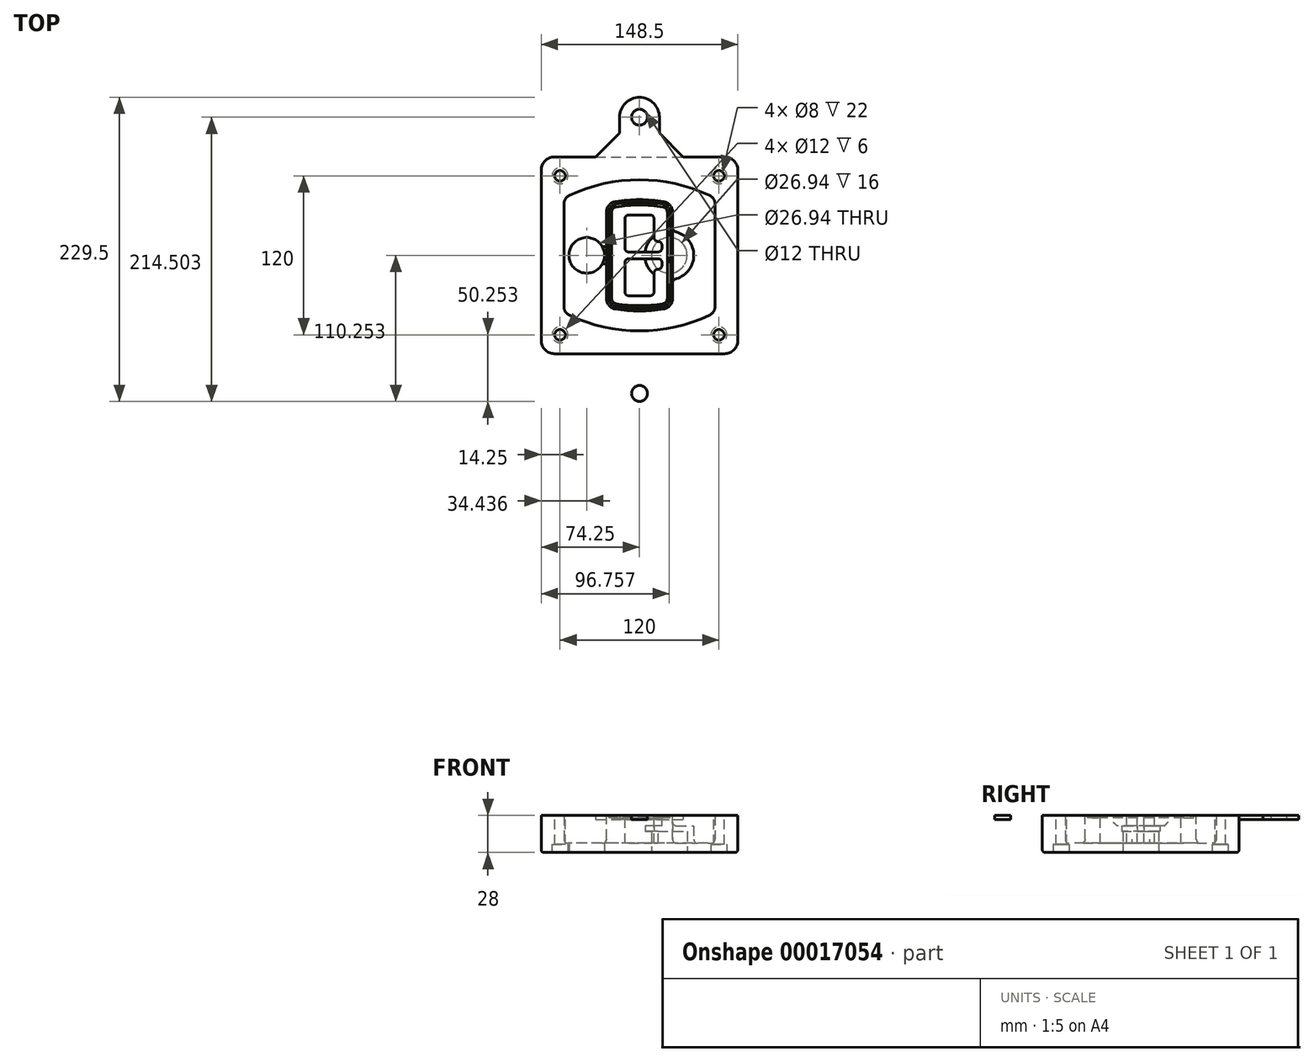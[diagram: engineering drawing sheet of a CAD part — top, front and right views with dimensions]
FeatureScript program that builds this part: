
annotation { "Feature Type Name" : "Feature", "Feature Type Description" : "" }
export const myFeature = defineFeature(function(context is Context, id is Id, definition is map)
    precondition{}
    {
        {
            var Q0;
            Q0=qCreatedBy(makeId("Top.planeOp"),FACE);
            var sketch = newSketch(context, id + "F0", { "sketchPlane" : qUnion([Q0])});
            skPoint(sketch, "E0.rect.middle", {"position": v(0, 0) * mm});
            skLineSegment(sketch, "E1.bottom", {"start": v(24.05, 28.38) * mm, "end": v(152.55, 28.38) * mm});
            skLineSegment(sketch, "E1.top", {"start": v(24.05, 176.88) * mm, "end": v(152.55, 176.88) * mm});
            skLineSegment(sketch, "E1.left", {"start": v(14.05, 38.38) * mm, "end": v(14.05, 166.88) * mm});
            skLineSegment(sketch, "E1.right", {"start": v(162.55, 38.38) * mm, "end": v(162.55, 166.88) * mm});
            skLineSegment(sketch, "E2", {"start": v(14.05, 176.88) * mm, "end": v(162.55, 28.38) * mm, "construction": true});
            skLineSegment(sketch, "E3", {"start": v(162.55, 176.88) * mm, "end": v(14.05, 28.38) * mm, "construction": true});
            skCircle(sketch, "E4", {"center": v(28.3, 162.63) * mm, "radius": 4 * mm});
            skCircle(sketch, "E5", {"center": v(148.3, 162.63) * mm, "radius": 4 * mm});
            skCircle(sketch, "E6", {"center": v(148.3, 42.63) * mm, "radius": 4 * mm});
            skCircle(sketch, "E7", {"center": v(28.3, 42.63) * mm, "radius": 4 * mm});
            skLineSegment(sketch, "E8", {"start": v(28.3, 162.63) * mm, "end": v(148.3, 162.63) * mm, "construction": true});
            skLineSegment(sketch, "E9", {"start": v(148.3, 162.63) * mm, "end": v(148.3, 42.63) * mm, "construction": true});
            skLineSegment(sketch, "E10", {"start": v(148.3, 42.63) * mm, "end": v(28.3, 42.63) * mm, "construction": true});
            skLineSegment(sketch, "E11", {"start": v(28.3, 42.63) * mm, "end": v(28.3, 162.63) * mm, "construction": true});
            skLineSegment(sketch, "E12", {"start": v(28.3, 141.46) * mm, "end": v(28.3, 63.8) * mm});
            skLineSegment(sketch, "E13", {"start": v(148.3, 141.46) * mm, "end": v(148.3, 63.8) * mm});
            skArc(sketch, "E14", {"start": v(142.56, 150.51) * mm, "mid": v(88.3, 162.63) * mm, "end": v(34.04, 150.51) * mm});
            skArc(sketch, "E15", {"start": v(34.04, 54.75) * mm, "mid": v(88.3, 42.63) * mm, "end": v(142.56, 54.75) * mm});
            skLineSegment(sketch, "E16", {"start": v(28.3, 102.63) * mm, "end": v(148.3, 102.63) * mm, "construction": true});
            skPoint(sketch, "E17.visualSharp", {"position": v(28.3, 57.63) * mm});
            skArc(sketch, "E17.filletArc", {"start": v(28.3, 63.8) * mm, "mid": v(29.86, 58.44) * mm, "end": v(34.04, 54.75) * mm});
            skPoint(sketch, "E18.visualSharp", {"position": v(28.3, 147.63) * mm});
            skArc(sketch, "E18.filletArc", {"start": v(34.04, 150.51) * mm, "mid": v(29.86, 146.82) * mm, "end": v(28.3, 141.46) * mm});
            skPoint(sketch, "E19.visualSharp", {"position": v(148.3, 147.63) * mm});
            skArc(sketch, "E19.filletArc", {"start": v(148.3, 141.46) * mm, "mid": v(146.74, 146.82) * mm, "end": v(142.56, 150.51) * mm});
            skPoint(sketch, "E20.visualSharp", {"position": v(148.3, 57.63) * mm});
            skArc(sketch, "E20.filletArc", {"start": v(142.56, 54.75) * mm, "mid": v(146.74, 58.44) * mm, "end": v(148.3, 63.8) * mm});
            skPoint(sketch, "E21.visualSharp", {"position": v(14.05, 176.88) * mm});
            skArc(sketch, "E21.filletArc", {"start": v(24.05, 176.88) * mm, "mid": v(16.98, 173.95) * mm, "end": v(14.05, 166.88) * mm});
            skPoint(sketch, "E22.visualSharp", {"position": v(162.55, 176.88) * mm});
            skArc(sketch, "E22.filletArc", {"start": v(162.55, 166.88) * mm, "mid": v(159.62, 173.95) * mm, "end": v(152.55, 176.88) * mm});
            skPoint(sketch, "E23.visualSharp", {"position": v(162.55, 28.38) * mm});
            skArc(sketch, "E23.filletArc", {"start": v(152.55, 28.38) * mm, "mid": v(159.62, 31.31) * mm, "end": v(162.55, 38.38) * mm});
            skPoint(sketch, "E24.visualSharp", {"position": v(14.05, 28.38) * mm});
            skArc(sketch, "E24.filletArc", {"start": v(14.05, 38.38) * mm, "mid": v(16.98, 31.31) * mm, "end": v(24.05, 28.38) * mm});
            skArc(sketch, "E25.0", {"start": v(145.3, 141.46) * mm, "mid": v(144.2, 145.22) * mm, "end": v(141.28, 147.8) * mm});
            skLineSegment(sketch, "E25.1", {"start": v(145.3, 141.46) * mm, "end": v(145.3, 63.8) * mm});
            skArc(sketch, "E25.2", {"start": v(141.28, 57.47) * mm, "mid": v(144.2, 60.05) * mm, "end": v(145.3, 63.8) * mm});
            skArc(sketch, "E25.3", {"start": v(35.32, 57.47) * mm, "mid": v(88.3, 45.63) * mm, "end": v(141.28, 57.47) * mm});
            skArc(sketch, "E25.4", {"start": v(31.3, 63.8) * mm, "mid": v(32.4, 60.05) * mm, "end": v(35.32, 57.47) * mm});
            skArc(sketch, "E25.5", {"start": v(141.28, 147.8) * mm, "mid": v(88.3, 159.63) * mm, "end": v(35.32, 147.8) * mm});
            skLineSegment(sketch, "E25.6", {"start": v(31.3, 141.46) * mm, "end": v(31.3, 63.8) * mm});
            skArc(sketch, "E25.7", {"start": v(35.32, 147.8) * mm, "mid": v(32.4, 145.22) * mm, "end": v(31.3, 141.46) * mm});
            skArc(sketch, "E26.0", {"start": v(32.34, 154.13) * mm, "mid": v(26.48, 148.97) * mm, "end": v(24.3, 141.46) * mm});
            skArc(sketch, "E26.1", {"start": v(144.26, 154.13) * mm, "mid": v(88.3, 166.63) * mm, "end": v(32.34, 154.13) * mm});
            skArc(sketch, "E26.2", {"start": v(152.3, 141.46) * mm, "mid": v(150.12, 148.97) * mm, "end": v(144.26, 154.13) * mm});
            skLineSegment(sketch, "E26.3", {"start": v(152.3, 141.46) * mm, "end": v(152.3, 63.8) * mm});
            skArc(sketch, "E26.4", {"start": v(144.26, 51.13) * mm, "mid": v(150.12, 56.3) * mm, "end": v(152.3, 63.8) * mm});
            skLineSegment(sketch, "E26.5", {"start": v(24.3, 141.46) * mm, "end": v(24.3, 63.8) * mm});
            skArc(sketch, "E26.6", {"start": v(32.34, 51.13) * mm, "mid": v(88.3, 38.63) * mm, "end": v(144.26, 51.13) * mm});
            skArc(sketch, "E26.7", {"start": v(24.3, 63.8) * mm, "mid": v(26.48, 56.3) * mm, "end": v(32.34, 51.13) * mm});
            skSolve(sketch);
        }
        {
            var Q0;
            Q0=makeQuery(id+"F0.imprint","IMPRINT",FACE,{"disambiguationData":[TD([[makeQuery(id+"F0.imprint","IMPRINT",EDGE,{"derivedFrom":sQuery(id+"F0.wireOp",EDGE,"E1.bottom")}),1.0]])]});
            var Q1;
            Q1=makeQuery(id+"F0.imprint","IMPRINT",FACE,{"disambiguationData":[TD([[makeQuery(id+"F0.imprint","IMPRINT",EDGE,{"derivedFrom":sQuery(id+"F0.wireOp",EDGE,"E12")}),1.0]])]});
            var Q2;
            Q2=makeQuery(id+"F0.imprint","IMPRINT",FACE,{"disambiguationData":[TD([[makeQuery(id+"F0.imprint","IMPRINT",EDGE,{"derivedFrom":sQuery(id+"F0.wireOp",EDGE,"E25.0")}),1.0]])]});
            var Q3;
            Q3=makeQuery(id+"F0.imprint","IMPRINT",FACE,{"disambiguationData":[TD([[makeQuery(id+"F0.imprint","IMPRINT",EDGE,{"derivedFrom":sQuery(id+"F0.wireOp",EDGE,"E12")}),-1.0]])]});
            extrude(context, id + "F1", {"entities" : qUnion([Q0, Q1, Q2, Q3]), "oppositeDirection" : true, "depth" : 25 * mm});
        }
        {
            var Q0;
            Q0=makeQuery(id+"F0.imprint","IMPRINT",FACE,{"disambiguationData":[TD([[makeQuery(id+"F0.imprint","IMPRINT",EDGE,{"derivedFrom":sQuery(id+"F0.wireOp",EDGE,"E12")}),1.0]])]});
            extrude(context, id + "F2", {"entities" : qUnion([Q0]), "operationType" : NewBodyOperationType.ADD, "depth" : 3 * mm});
        }
        {
            var Q0;
            Q0=makeQuery(id+"F0.imprint","IMPRINT",FACE,{"disambiguationData":[TD([[makeQuery(id+"F0.imprint","IMPRINT",EDGE,{"derivedFrom":sQuery(id+"F0.wireOp",EDGE,"E25.0")}),1.0]])]});
            extrude(context, id + "F3", {"entities" : qUnion([Q0]), "operationType" : NewBodyOperationType.REMOVE, "oppositeDirection" : true, "depth" : 18 * mm});
        }
        {
            var Q0;
            Q0=makeQuery(id+"F2.opExtrude","CAP_FACE",FACE,{"disambiguationData":[OSD([sQuery(id+"F0.wireOp",EDGE,"E12"),sQuery(id+"F0.wireOp",EDGE,"E13"),sQuery(id+"F0.wireOp",EDGE,"E14"),sQuery(id+"F0.wireOp",EDGE,"E15"),sQuery(id+"F0.wireOp",EDGE,"E17.filletArc"),sQuery(id+"F0.wireOp",EDGE,"E18.filletArc"),sQuery(id+"F0.wireOp",EDGE,"E19.filletArc"),sQuery(id+"F0.wireOp",EDGE,"E20.filletArc"),sQuery(id+"F0.wireOp",EDGE,"E25.0"),sQuery(id+"F0.wireOp",EDGE,"E25.1"),sQuery(id+"F0.wireOp",EDGE,"E25.2"),sQuery(id+"F0.wireOp",EDGE,"E25.3"),sQuery(id+"F0.wireOp",EDGE,"E25.4"),sQuery(id+"F0.wireOp",EDGE,"E25.5"),sQuery(id+"F0.wireOp",EDGE,"E25.6"),sQuery(id+"F0.wireOp",EDGE,"E25.7")])],"isStart":false});
            var sketch = newSketch(context, id + "F4", { "sketchPlane" : qUnion([Q0])});
            skArc(sketch, "E27.0", {"start": v(69.96, 62.18) * mm, "mid": v(88.3, 60.63) * mm, "end": v(106.64, 62.18) * mm});
            skArc(sketch, "E28.0", {"start": v(106.64, 143.09) * mm, "mid": v(88.3, 144.63) * mm, "end": v(69.96, 143.09) * mm});
            skLineSegment(sketch, "E29", {"start": v(63.3, 135.2) * mm, "end": v(63.3, 70.07) * mm});
            skLineSegment(sketch, "E30", {"start": v(113.3, 135.2) * mm, "end": v(113.3, 70.07) * mm});
            skLineSegment(sketch, "E31", {"start": v(63.3, 141.74) * mm, "end": v(113.3, 141.74) * mm, "construction": true});
            skLineSegment(sketch, "E32", {"start": v(63.3, 63.52) * mm, "end": v(113.3, 63.52) * mm, "construction": true});
            skPoint(sketch, "E33.visualSharp", {"position": v(63.3, 141.74) * mm});
            skArc(sketch, "E33.filletArc", {"start": v(69.96, 143.09) * mm, "mid": v(65.19, 140.36) * mm, "end": v(63.3, 135.2) * mm});
            skPoint(sketch, "E34.visualSharp", {"position": v(113.3, 141.74) * mm});
            skArc(sketch, "E34.filletArc", {"start": v(113.3, 135.2) * mm, "mid": v(111.41, 140.36) * mm, "end": v(106.64, 143.09) * mm});
            skPoint(sketch, "E35.visualSharp", {"position": v(113.3, 63.52) * mm});
            skArc(sketch, "E35.filletArc", {"start": v(106.64, 62.18) * mm, "mid": v(111.41, 64.9) * mm, "end": v(113.3, 70.07) * mm});
            skPoint(sketch, "E36.visualSharp", {"position": v(63.3, 63.52) * mm});
            skArc(sketch, "E36.filletArc", {"start": v(63.3, 70.07) * mm, "mid": v(65.19, 64.9) * mm, "end": v(69.96, 62.18) * mm});
            skArc(sketch, "E37.0", {"start": v(141.28, 147.8) * mm, "mid": v(88.3, 159.63) * mm, "end": v(35.32, 147.8) * mm});
            skArc(sketch, "E37.1", {"start": v(35.32, 147.8) * mm, "mid": v(32.4, 145.22) * mm, "end": v(31.3, 141.46) * mm});
            skLineSegment(sketch, "E37.2", {"start": v(31.3, 141.46) * mm, "end": v(31.3, 63.8) * mm});
            skArc(sketch, "E37.3", {"start": v(31.3, 63.8) * mm, "mid": v(32.4, 60.05) * mm, "end": v(35.32, 57.47) * mm});
            skArc(sketch, "E37.4", {"start": v(35.32, 57.47) * mm, "mid": v(88.3, 45.63) * mm, "end": v(141.28, 57.47) * mm});
            skArc(sketch, "E37.5", {"start": v(141.28, 57.47) * mm, "mid": v(144.2, 60.05) * mm, "end": v(145.3, 63.8) * mm});
            skLineSegment(sketch, "E37.6", {"start": v(145.3, 141.46) * mm, "end": v(145.3, 63.8) * mm});
            skArc(sketch, "E37.7", {"start": v(145.3, 141.46) * mm, "mid": v(144.2, 145.22) * mm, "end": v(141.28, 147.8) * mm});
            skLineSegment(sketch, "E38.0", {"start": v(111.3, 135.2) * mm, "end": v(111.3, 70.07) * mm});
            skArc(sketch, "E38.1", {"start": v(106.3, 64.15) * mm, "mid": v(109.88, 66.2) * mm, "end": v(111.3, 70.07) * mm});
            skArc(sketch, "E38.2", {"start": v(70.3, 64.15) * mm, "mid": v(88.3, 62.63) * mm, "end": v(106.3, 64.15) * mm});
            skArc(sketch, "E38.3", {"start": v(65.3, 70.07) * mm, "mid": v(66.72, 66.2) * mm, "end": v(70.3, 64.15) * mm});
            skLineSegment(sketch, "E38.4", {"start": v(65.3, 135.2) * mm, "end": v(65.3, 70.07) * mm});
            skArc(sketch, "E38.5", {"start": v(111.3, 135.2) * mm, "mid": v(109.88, 139.07) * mm, "end": v(106.3, 141.11) * mm});
            skArc(sketch, "E38.6", {"start": v(70.3, 141.11) * mm, "mid": v(66.72, 139.07) * mm, "end": v(65.3, 135.2) * mm});
            skArc(sketch, "E38.7", {"start": v(106.3, 141.11) * mm, "mid": v(88.3, 142.63) * mm, "end": v(70.3, 141.11) * mm});
            skArc(sketch, "E39.0", {"start": v(109.3, 135.2) * mm, "mid": v(108.36, 137.78) * mm, "end": v(105.97, 139.14) * mm});
            skLineSegment(sketch, "E39.1", {"start": v(109.3, 135.2) * mm, "end": v(109.3, 70.07) * mm});
            skArc(sketch, "E39.2", {"start": v(105.97, 66.12) * mm, "mid": v(108.36, 67.49) * mm, "end": v(109.3, 70.07) * mm});
            skArc(sketch, "E39.3", {"start": v(70.63, 66.12) * mm, "mid": v(88.3, 64.63) * mm, "end": v(105.97, 66.12) * mm});
            skArc(sketch, "E39.4", {"start": v(67.3, 70.07) * mm, "mid": v(68.24, 67.49) * mm, "end": v(70.63, 66.12) * mm});
            skArc(sketch, "E39.5", {"start": v(105.97, 139.14) * mm, "mid": v(88.3, 140.63) * mm, "end": v(70.63, 139.14) * mm});
            skLineSegment(sketch, "E39.6", {"start": v(67.3, 135.2) * mm, "end": v(67.3, 70.07) * mm});
            skArc(sketch, "E39.7", {"start": v(70.63, 139.14) * mm, "mid": v(68.24, 137.78) * mm, "end": v(67.3, 135.2) * mm});
            skLineSegment(sketch, "E40", {"start": v(63.3, 102.63) * mm, "end": v(113.3, 102.63) * mm, "construction": true});
            skLineSegment(sketch, "E41", {"start": v(77.3, 108.13) * mm, "end": v(77.3, 130.13) * mm});
            skLineSegment(sketch, "E42", {"start": v(80.3, 133.13) * mm, "end": v(96.3, 133.13) * mm});
            skLineSegment(sketch, "E43", {"start": v(99.3, 130.13) * mm, "end": v(99.3, 116.13) * mm});
            skLineSegment(sketch, "E44", {"start": v(102.3, 113.13) * mm, "end": v(102.3, 113.13) * mm});
            skLineSegment(sketch, "E45", {"start": v(105.3, 110.13) * mm, "end": v(105.3, 108.13) * mm});
            skLineSegment(sketch, "E46", {"start": v(102.3, 105.13) * mm, "end": v(80.3, 105.13) * mm});
            skPoint(sketch, "E47.visualSharp", {"position": v(77.3, 133.13) * mm});
            skArc(sketch, "E47.filletArc", {"start": v(80.3, 133.13) * mm, "mid": v(78.18, 132.25) * mm, "end": v(77.3, 130.13) * mm});
            skPoint(sketch, "E48.visualSharp", {"position": v(99.3, 133.13) * mm});
            skArc(sketch, "E48.filletArc", {"start": v(99.3, 130.13) * mm, "mid": v(98.42, 132.25) * mm, "end": v(96.3, 133.13) * mm});
            skPoint(sketch, "E49.visualSharp", {"position": v(99.3, 113.13) * mm});
            skArc(sketch, "E49.filletArc", {"start": v(99.3, 116.13) * mm, "mid": v(100.18, 114.01) * mm, "end": v(102.3, 113.13) * mm});
            skPoint(sketch, "E50.visualSharp", {"position": v(105.3, 113.13) * mm});
            skArc(sketch, "E50.filletArc", {"start": v(105.3, 110.13) * mm, "mid": v(104.42, 112.25) * mm, "end": v(102.3, 113.13) * mm});
            skPoint(sketch, "E51.visualSharp", {"position": v(105.3, 105.13) * mm});
            skArc(sketch, "E51.filletArc", {"start": v(102.3, 105.13) * mm, "mid": v(104.42, 106.01) * mm, "end": v(105.3, 108.13) * mm});
            skPoint(sketch, "E52.visualSharp", {"position": v(77.3, 105.13) * mm});
            skArc(sketch, "E52.filletArc", {"start": v(77.3, 108.13) * mm, "mid": v(78.18, 106.01) * mm, "end": v(80.3, 105.13) * mm});
            skLineSegment(sketch, "E53.0.MirrorCS", {"start": v(102.3, 100.13) * mm, "end": v(80.3, 100.13) * mm});
            skArc(sketch, "E54.0.MirrorCS", {"start": v(77.3, 97.13) * mm, "mid": v(78.18, 99.25) * mm, "end": v(80.3, 100.13) * mm});
            skLineSegment(sketch, "E55.0.MirrorCS", {"start": v(77.3, 97.13) * mm, "end": v(77.3, 75.13) * mm});
            skArc(sketch, "E56.0.MirrorCS", {"start": v(80.3, 72.13) * mm, "mid": v(78.18, 73.01) * mm, "end": v(77.3, 75.13) * mm});
            skLineSegment(sketch, "E57.0.MirrorCS", {"start": v(80.3, 72.13) * mm, "end": v(96.3, 72.13) * mm});
            skArc(sketch, "E58.0.MirrorCS", {"start": v(99.3, 75.13) * mm, "mid": v(98.42, 73.01) * mm, "end": v(96.3, 72.13) * mm});
            skLineSegment(sketch, "E59.0.MirrorCS", {"start": v(99.3, 75.13) * mm, "end": v(99.3, 89.13) * mm});
            skArc(sketch, "E60.0.MirrorCS", {"start": v(99.3, 89.13) * mm, "mid": v(100.18, 91.25) * mm, "end": v(102.3, 92.13) * mm});
            skArc(sketch, "E61.0.MirrorCS", {"start": v(105.3, 95.13) * mm, "mid": v(104.42, 93.01) * mm, "end": v(102.3, 92.13) * mm});
            skLineSegment(sketch, "E62.0.MirrorCS", {"start": v(105.3, 95.13) * mm, "end": v(105.3, 97.13) * mm});
            skArc(sketch, "E63.0.MirrorCS", {"start": v(102.3, 100.13) * mm, "mid": v(104.42, 99.25) * mm, "end": v(105.3, 97.13) * mm});
            skSolve(sketch);
        }
        {
            var Q0;
            Q0=makeQuery(id+"F4.imprint","IMPRINT",FACE,{"disambiguationData":[TD([[makeQuery(id+"F4.imprint","IMPRINT",EDGE,{"derivedFrom":sQuery(id+"F4.wireOp",EDGE,"E27.0")}),1.0]])]});
            var Q1;
            Q1=makeQuery(id+"F4.imprint","IMPRINT",FACE,{"disambiguationData":[TD([[makeQuery(id+"F4.imprint","IMPRINT",EDGE,{"derivedFrom":sQuery(id+"F4.wireOp",EDGE,"E38.0")}),-1.0]])]});
            var Q2;
            Q2=makeQuery(id+"F4.imprint","IMPRINT",FACE,{"disambiguationData":[TD([[makeQuery(id+"F4.imprint","IMPRINT",EDGE,{"derivedFrom":sQuery(id+"F4.wireOp",EDGE,"E39.0")}),1.0]])]});
            extrude(context, id + "F5", {"entities" : qUnion([Q0, Q1, Q2]), "operationType" : NewBodyOperationType.ADD, "endBound" : BoundingType.UP_TO_NEXT, "oppositeDirection" : true, "depth" : 25 * mm});
        }
        {
            var Q0;
            Q0=makeQuery(id+"F4.imprint","IMPRINT",FACE,{"disambiguationData":[TD([[makeQuery(id+"F4.imprint","IMPRINT",EDGE,{"derivedFrom":sQuery(id+"F4.wireOp",EDGE,"E38.0")}),-1.0]])]});
            extrude(context, id + "F6", {"entities" : qUnion([Q0]), "operationType" : NewBodyOperationType.REMOVE, "oppositeDirection" : true, "depth" : 2 * mm});
        }
        {
            var Q0;
            Q0=makeQuery(id+"F1.opExtrude","CAP_FACE",FACE,{"disambiguationData":[OSD([sQuery(id+"F0.wireOp",EDGE,"E1.bottom"),sQuery(id+"F0.wireOp",EDGE,"E1.top"),sQuery(id+"F0.wireOp",EDGE,"E1.left"),sQuery(id+"F0.wireOp",EDGE,"E1.right"),sQuery(id+"F0.wireOp",EDGE,"E4"),sQuery(id+"F0.wireOp",EDGE,"E5"),sQuery(id+"F0.wireOp",EDGE,"E6"),sQuery(id+"F0.wireOp",EDGE,"E7"),sQuery(id+"F0.wireOp",EDGE,"E21.filletArc"),sQuery(id+"F0.wireOp",EDGE,"E22.filletArc"),sQuery(id+"F0.wireOp",EDGE,"E23.filletArc"),sQuery(id+"F0.wireOp",EDGE,"E24.filletArc")])],"isStart":false});
            var sketch = newSketch(context, id + "F7", { "sketchPlane" : qUnion([Q0])});
            skCircle(sketch, "E64", {"center": v(110.8, -102.63) * mm, "radius": 13.47 * mm});
            skCircle(sketch, "E65", {"center": v(48.49, -102.63) * mm, "radius": 13.47 * mm});
            skLineSegment(sketch, "E66", {"start": v(162.55, -102.63) * mm, "end": v(14.05, -102.63) * mm});
            skCircle(sketch, "E67", {"center": v(110.8, -102.63) * mm, "radius": 18.47 * mm});
            skCircle(sketch, "E68", {"center": v(148.3, -162.63) * mm, "radius": 6 * mm});
            skCircle(sketch, "E69", {"center": v(28.3, -162.63) * mm, "radius": 6 * mm});
            skCircle(sketch, "E70", {"center": v(28.3, -42.63) * mm, "radius": 6 * mm});
            skCircle(sketch, "E71", {"center": v(148.3, -42.63) * mm, "radius": 6 * mm});
            skSolve(sketch);
        }
        {
            var Q0;
            {var subQ1=sQuery(id+"F7.wireOp",EDGE,"E66");var subQ4=sQuery(id+"F7.wireOp",EDGE,"E64");var subQ6=makeQuery(id+"F7.imprint","INTERSECT",VERTEX,{"disambiguationData":[OD(0.0)],"derivedFrom":[subQ4,subQ1]});Q0=makeQuery(id+"F7.imprint","IMPRINT",FACE,{"disambiguationData":[TD([[makeQuery(id+"F7.imprint","IMPRINT",EDGE,{"disambiguationData":[TD([[subQ6,-1.0]])],"derivedFrom":subQ4}),-1.0]])]});}
            var Q1;
            {var subQ0=sQuery(id+"F7.wireOp",EDGE,"E66");var subQ1=sQuery(id+"F7.wireOp",EDGE,"E64");var subQ3=makeQuery(id+"F7.imprint","INTERSECT",VERTEX,{"disambiguationData":[OD(0.0)],"derivedFrom":[subQ1,subQ0]});Q1=makeQuery(id+"F7.imprint","IMPRINT",FACE,{"disambiguationData":[TD([[makeQuery(id+"F7.imprint","IMPRINT",EDGE,{"disambiguationData":[TD([[subQ3,-1.0]])],"derivedFrom":subQ1}),1.0]])]});}
            var Q2;
            {var subQ0=sQuery(id+"F7.wireOp",EDGE,"E66");var subQ1=sQuery(id+"F7.wireOp",EDGE,"E64");var subQ3=makeQuery(id+"F7.imprint","INTERSECT",VERTEX,{"disambiguationData":[OD(0.0)],"derivedFrom":[subQ1,subQ0]});Q2=makeQuery(id+"F7.imprint","IMPRINT",FACE,{"disambiguationData":[TD([[makeQuery(id+"F7.imprint","IMPRINT",EDGE,{"disambiguationData":[TD([[subQ3,1.0]])],"derivedFrom":subQ1}),1.0]])]});}
            var Q3;
            {var subQ1=sQuery(id+"F7.wireOp",EDGE,"E66");var subQ4=sQuery(id+"F7.wireOp",EDGE,"E64");var subQ6=makeQuery(id+"F7.imprint","INTERSECT",VERTEX,{"disambiguationData":[OD(0.0)],"derivedFrom":[subQ4,subQ1]});Q3=makeQuery(id+"F7.imprint","IMPRINT",FACE,{"disambiguationData":[TD([[makeQuery(id+"F7.imprint","IMPRINT",EDGE,{"disambiguationData":[TD([[subQ6,1.0]])],"derivedFrom":subQ4}),-1.0]])]});}
            extrude(context, id + "F8", {"entities" : qUnion([Q0, Q1, Q2, Q3]), "operationType" : NewBodyOperationType.ADD, "oppositeDirection" : true, "depth" : 20 * mm});
        }
        {
            var Q0;
            {var subQ0=sQuery(id+"F7.wireOp",EDGE,"E66");var subQ1=sQuery(id+"F7.wireOp",EDGE,"E64");var subQ3=makeQuery(id+"F7.imprint","INTERSECT",VERTEX,{"disambiguationData":[OD(0.0)],"derivedFrom":[subQ1,subQ0]});Q0=makeQuery(id+"F7.imprint","IMPRINT",FACE,{"disambiguationData":[TD([[makeQuery(id+"F7.imprint","IMPRINT",EDGE,{"disambiguationData":[TD([[subQ3,-1.0]])],"derivedFrom":subQ1}),1.0]])]});}
            var Q1;
            {var subQ0=sQuery(id+"F7.wireOp",EDGE,"E66");var subQ1=sQuery(id+"F7.wireOp",EDGE,"E64");var subQ3=makeQuery(id+"F7.imprint","INTERSECT",VERTEX,{"disambiguationData":[OD(0.0)],"derivedFrom":[subQ1,subQ0]});Q1=makeQuery(id+"F7.imprint","IMPRINT",FACE,{"disambiguationData":[TD([[makeQuery(id+"F7.imprint","IMPRINT",EDGE,{"disambiguationData":[TD([[subQ3,1.0]])],"derivedFrom":subQ1}),1.0]])]});}
            extrude(context, id + "F9", {"entities" : qUnion([Q0, Q1]), "operationType" : NewBodyOperationType.REMOVE, "oppositeDirection" : true, "depth" : 16 * mm});
        }
        {
            var Q0;
            {var subQ0=sQuery(id+"F7.wireOp",EDGE,"E66");var subQ1=sQuery(id+"F7.wireOp",EDGE,"E65");var subQ3=makeQuery(id+"F7.imprint","INTERSECT",VERTEX,{"disambiguationData":[OD(0.0)],"derivedFrom":[subQ1,subQ0]});Q0=makeQuery(id+"F7.imprint","IMPRINT",FACE,{"disambiguationData":[TD([[makeQuery(id+"F7.imprint","IMPRINT",EDGE,{"disambiguationData":[TD([[subQ3,-1.0]])],"derivedFrom":subQ1}),1.0]])]});}
            var Q1;
            {var subQ0=sQuery(id+"F7.wireOp",EDGE,"E66");var subQ1=sQuery(id+"F7.wireOp",EDGE,"E65");var subQ3=makeQuery(id+"F7.imprint","INTERSECT",VERTEX,{"disambiguationData":[OD(0.0)],"derivedFrom":[subQ1,subQ0]});Q1=makeQuery(id+"F7.imprint","IMPRINT",FACE,{"disambiguationData":[TD([[makeQuery(id+"F7.imprint","IMPRINT",EDGE,{"disambiguationData":[TD([[subQ3,1.0]])],"derivedFrom":subQ1}),1.0]])]});}
            extrude(context, id + "F10", {"entities" : qUnion([Q0, Q1]), "operationType" : NewBodyOperationType.REMOVE, "oppositeDirection" : true, "depth" : 25 * mm});
        }
        {
            var Q0;
            Q0=makeQuery(id+"F7.imprint","IMPRINT",FACE,{"disambiguationData":[TD([[makeQuery(id+"F7.imprint","IMPRINT",EDGE,{"derivedFrom":sQuery(id+"F7.wireOp",EDGE,"E68")}),1.0]])]});
            var Q1;
            Q1=makeQuery(id+"F7.imprint","IMPRINT",FACE,{"disambiguationData":[TD([[makeQuery(id+"F7.imprint","IMPRINT",EDGE,{"derivedFrom":makeQuery(id+"F1.opExtrude","CAP_EDGE",EDGE,{"disambiguationData":[OSD([sQuery(id+"F0.wireOp",EDGE,"E5")])],"isStart":false})}),-1.0]])]});
            var Q2;
            Q2=makeQuery(id+"F7.imprint","IMPRINT",FACE,{"disambiguationData":[TD([[makeQuery(id+"F7.imprint","IMPRINT",EDGE,{"derivedFrom":sQuery(id+"F7.wireOp",EDGE,"E69")}),1.0]])]});
            var Q3;
            Q3=makeQuery(id+"F7.imprint","IMPRINT",FACE,{"disambiguationData":[TD([[makeQuery(id+"F7.imprint","IMPRINT",EDGE,{"derivedFrom":makeQuery(id+"F1.opExtrude","CAP_EDGE",EDGE,{"disambiguationData":[OSD([sQuery(id+"F0.wireOp",EDGE,"E4")])],"isStart":false})}),-1.0]])]});
            var Q4;
            Q4=makeQuery(id+"F7.imprint","IMPRINT",FACE,{"disambiguationData":[TD([[makeQuery(id+"F7.imprint","IMPRINT",EDGE,{"derivedFrom":sQuery(id+"F7.wireOp",EDGE,"E70")}),1.0]])]});
            var Q5;
            Q5=makeQuery(id+"F7.imprint","IMPRINT",FACE,{"disambiguationData":[TD([[makeQuery(id+"F7.imprint","IMPRINT",EDGE,{"derivedFrom":makeQuery(id+"F1.opExtrude","CAP_EDGE",EDGE,{"disambiguationData":[OSD([sQuery(id+"F0.wireOp",EDGE,"E7")])],"isStart":false})}),-1.0]])]});
            var Q6;
            Q6=makeQuery(id+"F7.imprint","IMPRINT",FACE,{"disambiguationData":[TD([[makeQuery(id+"F7.imprint","IMPRINT",EDGE,{"derivedFrom":sQuery(id+"F7.wireOp",EDGE,"E71")}),1.0]])]});
            var Q7;
            Q7=makeQuery(id+"F7.imprint","IMPRINT",FACE,{"disambiguationData":[TD([[makeQuery(id+"F7.imprint","IMPRINT",EDGE,{"derivedFrom":makeQuery(id+"F1.opExtrude","CAP_EDGE",EDGE,{"disambiguationData":[OSD([sQuery(id+"F0.wireOp",EDGE,"E6")])],"isStart":false})}),-1.0]])]});
            extrude(context, id + "F11", {"entities" : qUnion([Q0, Q1, Q2, Q3, Q4, Q5, Q6, Q7]), "operationType" : NewBodyOperationType.REMOVE, "oppositeDirection" : true, "depth" : 6 * mm});
        }
        {
            var Q0;
            Q0=makeQuery(id+"F9.boolean.opBoolean","COPY",FACE,{"derivedFrom":makeQuery(id+"F9.opExtrude","CAP_FACE",FACE,{"disambiguationData":[OSD([sQuery(id+"F7.wireOp",EDGE,"E64")])],"isStart":false})});
            var sketch = newSketch(context, id + "F12", { "sketchPlane" : qUnion([Q0])});
            skArc(sketch, "E72.0", {"start": v(99.3, -88.19) * mm, "mid": v(94.75, -93.5) * mm, "end": v(92.5, -100.13) * mm});
            skArc(sketch, "E72.1", {"start": v(92.5, -105.13) * mm, "mid": v(94.75, -111.76) * mm, "end": v(99.3, -117.08) * mm});
            skLineSegment(sketch, "E73", {"start": v(92.5, -105.13) * mm, "end": v(102.3, -105.13) * mm});
            skLineSegment(sketch, "E74.0", {"start": v(102.3, -100.13) * mm, "end": v(92.5, -100.13) * mm});
            skArc(sketch, "E74.1", {"start": v(102.3, -100.13) * mm, "mid": v(104.42, -99.25) * mm, "end": v(105.3, -97.13) * mm});
            skLineSegment(sketch, "E74.2", {"start": v(105.3, -95.13) * mm, "end": v(105.3, -97.13) * mm});
            skArc(sketch, "E74.3", {"start": v(105.3, -95.13) * mm, "mid": v(104.42, -93.01) * mm, "end": v(102.3, -92.13) * mm});
            skArc(sketch, "E74.4", {"start": v(99.3, -89.13) * mm, "mid": v(100.18, -91.25) * mm, "end": v(102.3, -92.13) * mm});
            skLineSegment(sketch, "E74.5", {"start": v(99.3, -88.19) * mm, "end": v(99.3, -89.13) * mm});
            skLineSegment(sketch, "E74.7", {"start": v(102.3, -105.13) * mm, "end": v(92.5, -105.13) * mm});
            skArc(sketch, "E74.8", {"start": v(102.3, -105.13) * mm, "mid": v(104.42, -106.01) * mm, "end": v(105.3, -108.13) * mm});
            skLineSegment(sketch, "E74.9", {"start": v(105.3, -110.13) * mm, "end": v(105.3, -108.13) * mm});
            skArc(sketch, "E74.10", {"start": v(105.3, -110.13) * mm, "mid": v(104.42, -112.25) * mm, "end": v(102.3, -113.13) * mm});
            skArc(sketch, "E74.11", {"start": v(99.3, -116.13) * mm, "mid": v(100.18, -114.01) * mm, "end": v(102.3, -113.13) * mm});
            skLineSegment(sketch, "E74.12", {"start": v(99.3, -117.08) * mm, "end": v(99.3, -116.13) * mm});
            skPoint(sketch, "E75.orphan", {"position": v(99.3, -130.13) * mm});
            skPoint(sketch, "E76.orphan", {"position": v(80.3, -105.13) * mm});
            skPoint(sketch, "E77.orphan", {"position": v(80.3, -100.13) * mm});
            skPoint(sketch, "E78.orphan", {"position": v(99.3, -75.13) * mm});
            skSolve(sketch);
        }
        {
            var Q0;
            {var subQ7=sQuery(id+"F12.wireOp",EDGE,"E72.0");var subQ14=sQuery(id+"F12.wireOp",EDGE,"E72.1");var subQ16=sQuery(id+"F12.wireOp",EDGE,"E74.1");var subQ18=sQuery(id+"F12.wireOp",EDGE,"E74.8");Q0=qUnion([makeQuery(id+"F12.imprint","IMPRINT",FACE,{"disambiguationData":[TD([[makeQuery(id+"F12.imprint","IMPRINT",EDGE,{"derivedFrom":subQ7}),1.0]])]}),makeQuery(id+"F12.imprint","IMPRINT",FACE,{"disambiguationData":[TD([[makeQuery(id+"F12.imprint","IMPRINT",EDGE,{"derivedFrom":subQ14}),1.0]])]}),makeQuery(id+"F12.imprint","IMPRINT",FACE,{"disambiguationData":[TD([[makeQuery(id+"F12.imprint","IMPRINT",EDGE,{"derivedFrom":subQ16}),1.0]])]}),makeQuery(id+"F12.imprint","IMPRINT",FACE,{"disambiguationData":[TD([[makeQuery(id+"F12.imprint","IMPRINT",EDGE,{"derivedFrom":subQ18}),-1.0]])]})]);}
            var Q1;
            Q1=makeQuery(id+"F5.boolean.opBoolean","SPLIT",FACE,{"disambiguationData":[TD([makeQuery(id+"F5.opExtrude","SWEPT_FACE",FACE,{"disambiguationData":[OSD([sQuery(id+"F4.wireOp",EDGE,"E41")])]})])],"derivedFrom":makeQuery(id+"F3.boolean.opBoolean","COPY",FACE,{"derivedFrom":makeQuery(id+"F3.opExtrude","CAP_FACE",FACE,{"disambiguationData":[OSD([sQuery(id+"F0.wireOp",EDGE,"E25.0"),sQuery(id+"F0.wireOp",EDGE,"E25.1"),sQuery(id+"F0.wireOp",EDGE,"E25.2"),sQuery(id+"F0.wireOp",EDGE,"E25.3"),sQuery(id+"F0.wireOp",EDGE,"E25.4"),sQuery(id+"F0.wireOp",EDGE,"E25.5"),sQuery(id+"F0.wireOp",EDGE,"E25.6"),sQuery(id+"F0.wireOp",EDGE,"E25.7")])],"isStart":false})})});
            extrude(context, id + "F13", {"entities" : qUnion([Q0]), "operationType" : NewBodyOperationType.REMOVE, "endBound" : BoundingType.UP_TO_SURFACE, "endBoundEntityFace" : qUnion([Q1]), "depth" : 25 * mm});
        }
        {
            var Q0;
            Q0=makeQuery(id+"F3.boolean.opBoolean","COPY",EDGE,{"derivedFrom":makeQuery(id+"F3.opExtrude","CAP_EDGE",EDGE,{"disambiguationData":[OSD([sQuery(id+"F0.wireOp",EDGE,"E25.6")])],"isStart":false})});
            var Q1;
            Q1=makeQuery(id+"F8.boolean.opBoolean","INTERSECT",EDGE,{"derivedFrom":[makeQuery(id+"F5.opExtrude","SWEPT_FACE",FACE,{"disambiguationData":[OSD([sQuery(id+"F4.wireOp",EDGE,"E30")])]}),makeQuery(id+"F8.opExtrude","CAP_FACE",FACE,{"disambiguationData":[OSD([sQuery(id+"F7.wireOp",EDGE,"E67")])],"isStart":false})]});
            var Q2;
            Q2=makeQuery(id+"F8.boolean.opBoolean","INTERSECT",EDGE,{"disambiguationData":[OD(1.0)],"derivedFrom":[makeQuery(id+"F5.opExtrude","SWEPT_FACE",FACE,{"disambiguationData":[OSD([sQuery(id+"F4.wireOp",EDGE,"E30")])]}),makeQuery(id+"F8.opExtrude","SWEPT_FACE",FACE,{"disambiguationData":[OSD([sQuery(id+"F7.wireOp",EDGE,"E67")])]})]});
            var Q3;
            {var subQ0=sQuery(id+"F4.wireOp",EDGE,"E30");Q3=makeQuery(id+"F8.boolean.opBoolean","SPLIT",EDGE,{"disambiguationData":[TD([makeQuery(id+"F5.opExtrude","SWEPT_FACE",FACE,{"disambiguationData":[OSD([sQuery(id+"F4.wireOp",EDGE,"E35.filletArc")])]})])],"derivedFrom":makeQuery(id+"F5.opExtrude","CAP_EDGE",EDGE,{"disambiguationData":[OSD([subQ0])],"isStart":false})});}
            var Q4;
            {var subQ0=sQuery(id+"F0.wireOp",EDGE,"E25.7");var subQ1=sQuery(id+"F0.wireOp",EDGE,"E25.1");var subQ2=sQuery(id+"F0.wireOp",EDGE,"E25.6");var subQ3=sQuery(id+"F0.wireOp",EDGE,"E25.5");var subQ4=sQuery(id+"F0.wireOp",EDGE,"E25.4");var subQ5=sQuery(id+"F0.wireOp",EDGE,"E25.0");var subQ6=sQuery(id+"F0.wireOp",EDGE,"E25.2");var subQ7=sQuery(id+"F0.wireOp",EDGE,"E25.3");Q4=makeQuery(id+"F8.boolean.opBoolean","INTERSECT",EDGE,{"derivedFrom":[makeQuery(id+"F5.boolean.opBoolean","SPLIT",FACE,{"disambiguationData":[TD([makeQuery(id+"F2.opExtrude","SWEPT_FACE",FACE,{"disambiguationData":[OSD([subQ5])]})])],"derivedFrom":makeQuery(id+"F3.boolean.opBoolean","COPY",FACE,{"derivedFrom":makeQuery(id+"F3.opExtrude","CAP_FACE",FACE,{"disambiguationData":[OSD([subQ5,subQ1,subQ6,subQ7,subQ4,subQ3,subQ2,subQ0])],"isStart":false})})}),makeQuery(id+"F8.opExtrude","SWEPT_FACE",FACE,{"disambiguationData":[OSD([sQuery(id+"F7.wireOp",EDGE,"E67")])]})]});}
            var Q5;
            Q5=makeQuery(id+"F8.boolean.opBoolean","INTERSECT",EDGE,{"disambiguationData":[OD(0.0)],"derivedFrom":[makeQuery(id+"F5.opExtrude","SWEPT_FACE",FACE,{"disambiguationData":[OSD([sQuery(id+"F4.wireOp",EDGE,"E30")])]}),makeQuery(id+"F8.opExtrude","SWEPT_FACE",FACE,{"disambiguationData":[OSD([sQuery(id+"F7.wireOp",EDGE,"E67")])]})]});
            fillet(context, id + "F14", {"entities" : qUnion([Q0, Q1, Q2, Q3, Q4, Q5]), "radius" : 3 * mm, "tangentPropagation" : true, "allowEdgeOverflow" : false});
        }
        {
            var Q0;
            Q0=makeQuery(id+"F1.opExtrude","CAP_EDGE",EDGE,{"disambiguationData":[OSD([sQuery(id+"F0.wireOp",EDGE,"E1.bottom")])],"isStart":false});
            fillet(context, id + "F15", {"entities" : qUnion([Q0]), "radius" : 2 * mm, "tangentPropagation" : true, "allowEdgeOverflow" : false});
        }
        {
            var Q0;
            {var subQ0=sQuery(id+"F0.wireOp",EDGE,"E1.bottom");var subQ1=sQuery(id+"F0.wireOp",EDGE,"E1.top");var subQ2=sQuery(id+"F0.wireOp",EDGE,"E1.left");var subQ3=sQuery(id+"F0.wireOp",EDGE,"E1.right");var subQ4=sQuery(id+"F0.wireOp",EDGE,"E4");var subQ5=sQuery(id+"F0.wireOp",EDGE,"E5");var subQ6=sQuery(id+"F0.wireOp",EDGE,"E6");var subQ7=sQuery(id+"F0.wireOp",EDGE,"E7");var subQ8=sQuery(id+"F0.wireOp",EDGE,"E21.filletArc");var subQ9=sQuery(id+"F0.wireOp",EDGE,"E22.filletArc");var subQ10=sQuery(id+"F0.wireOp",EDGE,"E23.filletArc");var subQ11=sQuery(id+"F0.wireOp",EDGE,"E24.filletArc");Q0=makeQuery(id+"F2.boolean.opBoolean","SPLIT",FACE,{"disambiguationData":[TD([makeQuery(id+"F1.opExtrude","SWEPT_FACE",FACE,{"disambiguationData":[OSD([subQ0])]})])],"derivedFrom":makeQuery(id+"F1.opExtrude","CAP_FACE",FACE,{"disambiguationData":[OSD([subQ0,subQ1,subQ2,subQ3,subQ4,subQ5,subQ6,subQ7,subQ8,subQ9,subQ10,subQ11])],"isStart":true})});}
            var sketch = newSketch(context, id + "F16", { "sketchPlane" : qUnion([Q0])});
            skLineSegment(sketch, "E79", {"start": v(55.3, 176.88) * mm, "end": v(73.3, 194.88) * mm});
            skLineSegment(sketch, "E80", {"start": v(73.3, 194.88) * mm, "end": v(73.3, 206.88) * mm});
            skLineSegment(sketch, "E81", {"start": v(103.3, 194.88) * mm, "end": v(121.3, 176.88) * mm});
            skArc(sketch, "E82", {"start": v(103.3, 206.88) * mm, "mid": v(88.3, 221.88) * mm, "end": v(73.3, 206.88) * mm});
            skLineSegment(sketch, "E83", {"start": v(88.3, 206.88) * mm, "end": v(88.3, 176.88) * mm, "construction": true});
            skLineSegment(sketch, "E84", {"start": v(55.3, 176.88) * mm, "end": v(121.3, 176.88) * mm});
            skLineSegment(sketch, "E85", {"start": v(103.3, 206.88) * mm, "end": v(103.3, 194.88) * mm});
            skCircle(sketch, "E86", {"center": v(88.3, 206.88) * mm, "radius": 6 * mm});
            skLineSegment(sketch, "E87", {"start": v(14.05, 102.63) * mm, "end": v(162.55, 102.63) * mm, "construction": true});
            skCircle(sketch, "E88.MirrorC", {"center": v(88.3, -1.62) * mm, "radius": 6 * mm});
            skLineSegment(sketch, "E89.MirrorCS", {"start": v(55.3, 28.38) * mm, "end": v(73.3, 10.38) * mm});
            skLineSegment(sketch, "E90.MirrorCS", {"start": v(73.3, 10.38) * mm, "end": v(73.3, -1.62) * mm});
            skLineSegment(sketch, "E91.MirrorCS", {"start": v(103.3, 10.38) * mm, "end": v(121.3, 28.38) * mm});
            skArc(sketch, "E92.MirrorCS", {"start": v(103.3, -1.62) * mm, "mid": v(88.3, -16.62) * mm, "end": v(73.3, -1.62) * mm});
            skLineSegment(sketch, "E93.MirrorCS", {"start": v(103.3, -1.62) * mm, "end": v(103.3, 10.38) * mm});
            skLineSegment(sketch, "E94.MirrorCS", {"start": v(55.3, 28.38) * mm, "end": v(121.3, 28.38) * mm});
            skLineSegment(sketch, "E95.MirrorCS", {"start": v(88.3, -1.62) * mm, "end": v(88.3, 28.38) * mm});
            skLineSegment(sketch, "E96.0", {"start": v(24.05, 176.88) * mm, "end": v(152.55, 176.88) * mm});
            skArc(sketch, "E97.0", {"start": v(162.55, 166.88) * mm, "mid": v(159.62, 173.95) * mm, "end": v(152.55, 176.88) * mm});
            skLineSegment(sketch, "E98.5", {"start": v(162.55, 38.38) * mm, "end": v(162.55, 166.88) * mm});
            skArc(sketch, "E99.6", {"start": v(152.55, 28.38) * mm, "mid": v(159.62, 31.31) * mm, "end": v(162.55, 38.38) * mm});
            skLineSegment(sketch, "E100.7", {"start": v(24.05, 28.38) * mm, "end": v(152.55, 28.38) * mm});
            skArc(sketch, "E101.8", {"start": v(14.05, 38.38) * mm, "mid": v(16.98, 31.31) * mm, "end": v(24.05, 28.38) * mm});
            skLineSegment(sketch, "E102.9", {"start": v(14.05, 38.38) * mm, "end": v(14.05, 166.88) * mm});
            skArc(sketch, "E103.10", {"start": v(24.05, 176.88) * mm, "mid": v(16.98, 173.95) * mm, "end": v(14.05, 166.88) * mm});
            skCircle(sketch, "E104.11", {"center": v(148.3, 162.63) * mm, "radius": 4 * mm});
            skCircle(sketch, "E105.12", {"center": v(28.3, 162.63) * mm, "radius": 4 * mm});
            skCircle(sketch, "E106.13", {"center": v(28.3, 42.63) * mm, "radius": 4 * mm});
            skCircle(sketch, "E107.14", {"center": v(148.3, 42.63) * mm, "radius": 4 * mm});
            skArc(sketch, "E108.0", {"start": v(142.56, 150.51) * mm, "mid": v(88.3, 162.63) * mm, "end": v(34.04, 150.51) * mm});
            skArc(sketch, "E109.0", {"start": v(34.04, 150.51) * mm, "mid": v(29.86, 146.82) * mm, "end": v(28.3, 141.46) * mm});
            skLineSegment(sketch, "E110.0", {"start": v(28.3, 141.46) * mm, "end": v(28.3, 63.8) * mm});
            skArc(sketch, "E111.0", {"start": v(34.04, 54.75) * mm, "mid": v(88.3, 42.63) * mm, "end": v(142.56, 54.75) * mm});
            skArc(sketch, "E112.0", {"start": v(28.3, 63.8) * mm, "mid": v(29.86, 58.44) * mm, "end": v(34.04, 54.75) * mm});
            skArc(sketch, "E113.0", {"start": v(142.56, 54.75) * mm, "mid": v(146.74, 58.44) * mm, "end": v(148.3, 63.8) * mm});
            skLineSegment(sketch, "E114.0", {"start": v(148.3, 141.46) * mm, "end": v(148.3, 63.8) * mm});
            skArc(sketch, "E115.0", {"start": v(148.3, 141.46) * mm, "mid": v(146.74, 146.82) * mm, "end": v(142.56, 150.51) * mm});
            skSolve(sketch);
        }
        {
            var Q0;
            {var subQ2=sQuery(id+"F16.wireOp",EDGE,"E79");Q0=makeQuery(id+"F16.imprint","IMPRINT",FACE,{"disambiguationData":[TD([[makeQuery(id+"F16.imprint","IMPRINT",EDGE,{"derivedFrom":subQ2}),-1.0]])]});}
            var Q1;
            {var subQ4=sQuery(id+"F16.wireOp",EDGE,"E97.0");Q1=makeQuery(id+"F16.imprint","IMPRINT",FACE,{"disambiguationData":[TD([[makeQuery(id+"F16.imprint","IMPRINT",EDGE,{"derivedFrom":subQ4}),1.0]])]});}
            var Q2;
            Q2=makeQuery(id+"F16.imprint","IMPRINT",FACE,{"disambiguationData":[TD([[makeQuery(id+"F16.imprint","IMPRINT",EDGE,{"derivedFrom":sQuery(id+"F16.wireOp",EDGE,"E88.MirrorC")}),1.0]])]});
            var Q3;
            Q3=makeQuery(id+"F2.opExtrude","CAP_FACE",FACE,{"disambiguationData":[OSD([sQuery(id+"F0.wireOp",EDGE,"E12"),sQuery(id+"F0.wireOp",EDGE,"E13"),sQuery(id+"F0.wireOp",EDGE,"E14"),sQuery(id+"F0.wireOp",EDGE,"E15"),sQuery(id+"F0.wireOp",EDGE,"E17.filletArc"),sQuery(id+"F0.wireOp",EDGE,"E18.filletArc"),sQuery(id+"F0.wireOp",EDGE,"E19.filletArc"),sQuery(id+"F0.wireOp",EDGE,"E20.filletArc"),sQuery(id+"F0.wireOp",EDGE,"E25.0"),sQuery(id+"F0.wireOp",EDGE,"E25.1"),sQuery(id+"F0.wireOp",EDGE,"E25.2"),sQuery(id+"F0.wireOp",EDGE,"E25.3"),sQuery(id+"F0.wireOp",EDGE,"E25.4"),sQuery(id+"F0.wireOp",EDGE,"E25.5"),sQuery(id+"F0.wireOp",EDGE,"E25.6"),sQuery(id+"F0.wireOp",EDGE,"E25.7")])],"isStart":false});
            extrude(context, id + "F17", {"entities" : qUnion([Q0, Q1, Q2]), "operationType" : NewBodyOperationType.ADD, "endBound" : BoundingType.UP_TO_SURFACE, "endBoundEntityFace" : qUnion([Q3]), "depth" : 25 * mm});
        }
    });
